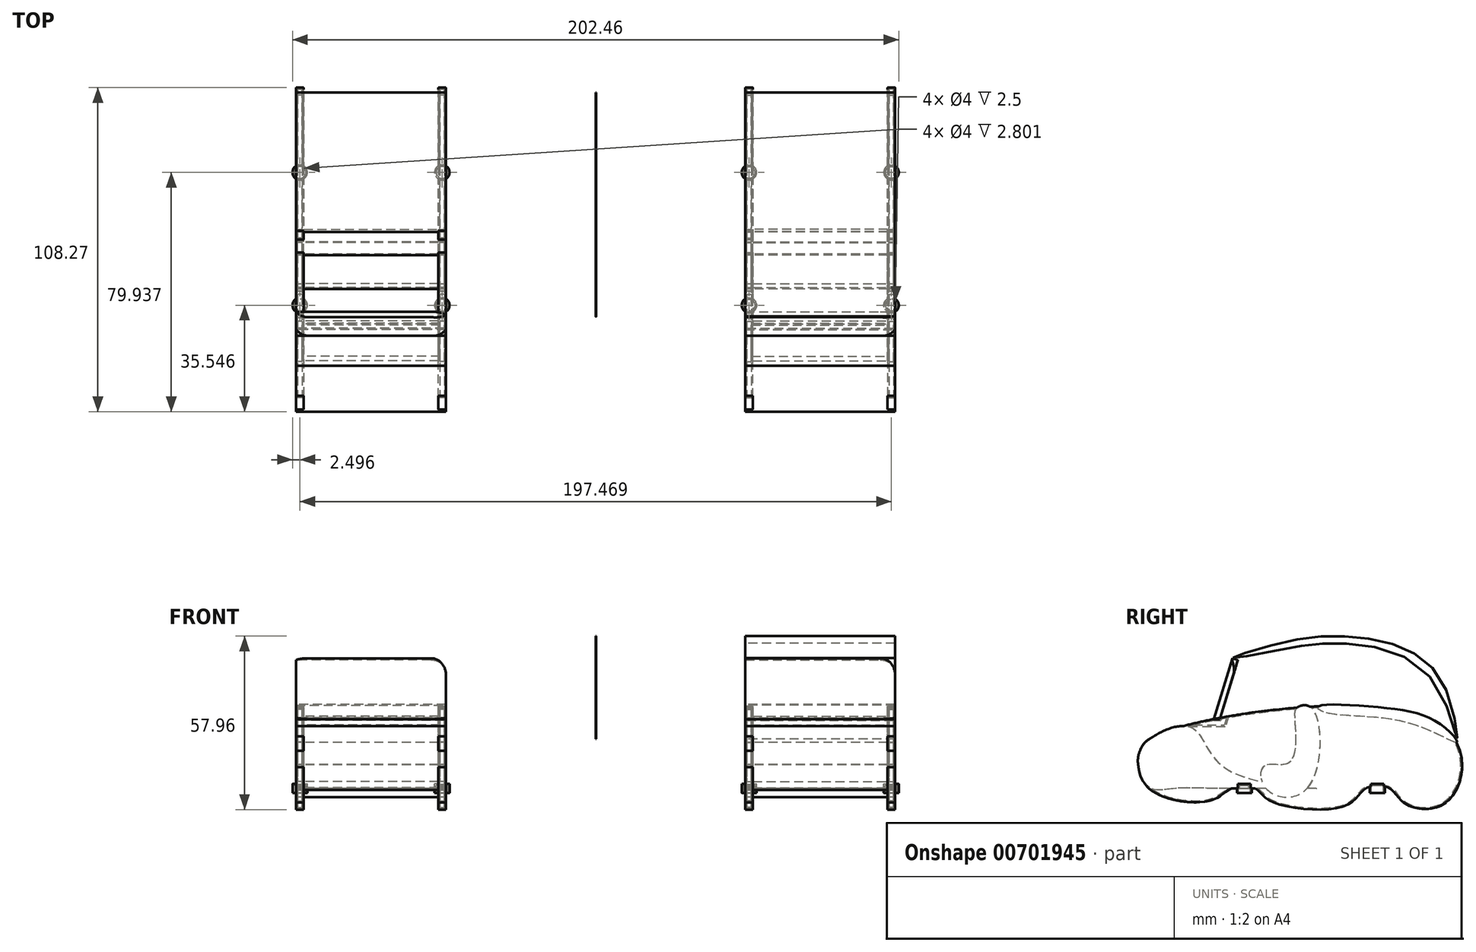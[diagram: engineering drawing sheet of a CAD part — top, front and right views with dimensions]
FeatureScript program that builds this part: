
annotation { "Feature Type Name" : "Feature", "Feature Type Description" : "" }
export const myFeature = defineFeature(function(context is Context, id is Id, definition is map)
    precondition{}
    {
        {
            var Q0;
            Q0=qCreatedBy(makeId("Right.planeOp"),FACE);
            var sketch = newSketch(context, id + "F0", { "sketchPlane" : qUnion([Q0])});
            skFitSpline(sketch, "E0", {"points": [v(-51.6, 18.76) * mm, v(-59.76, 11.07) * mm, v(-56.5, 0) * mm, v(-36, -4.08) * mm, v(-28.77, 0) * mm, v(-20.85, 0) * mm, v(-16.2, -4.08) * mm, v(9.44, -5.7) * mm, v(15.96, 0) * mm, v(23.88, 0) * mm, v(29, -5) * mm, v(43.22, -4.31) * mm, v(42.05, 20.39) * mm, v(-51.6, 18.76) * mm]});
            skLineSegment(sketch, "E1", {"start": v(-34.79, 23.16) * mm, "end": v(-28.6, 43.48) * mm});
            skLineSegment(sketch, "E2", {"start": v(-28.6, 43.48) * mm, "end": v(-26.72, 42.9) * mm});
            skLineSegment(sketch, "E3", {"start": v(-26.72, 42.9) * mm, "end": v(-32.74, 23.16) * mm});
            skLineSegment(sketch, "E4", {"start": v(-34.79, 23.16) * mm, "end": v(-32.74, 23.16) * mm});
            skSolve(sketch);
        }
        {
            var Q0;
            {var subQ0=sQuery(id+"F0.wireOp",EDGE,"E4");Q0=makeQuery(id+"F0.imprint","IMPRINT",FACE,{"disambiguationData":[TD([[makeQuery(id+"F0.imprint","IMPRINT",EDGE,{"derivedFrom":subQ0}),-1.0]])]});}
            var Q1;
            {var subQ0=sQuery(id+"F0.wireOp",EDGE,"E1");Q1=makeQuery(id+"F0.imprint","IMPRINT",FACE,{"disambiguationData":[TD([[makeQuery(id+"F0.imprint","IMPRINT",EDGE,{"derivedFrom":subQ0}),-1.0]])]});}
            extrude(context, id + "F1", {"entities" : qUnion([Q0, Q1]), "endBound" : BoundingType.SYMMETRIC, "depth" : 50 * mm, "offsetDistance" : 25 * mm});
        }
        {
            var Q0;
            {var subQ0=sQuery(id+"F0.wireOp",EDGE,"E0");Q0=makeQuery(id+"F1.opExtrude","SWEPT_FACE",FACE,{"disambiguationData":[OSD([subQ0]),TDD([makeQuery(id+"F0.imprint","IMPRINT",EDGE,{"disambiguationData":[TD([[makeQuery(id+"F0.imprint","INTERSECT",VERTEX,{"derivedFrom":[subQ0,sQuery(id+"F0.wireOp",EDGE,"E3")]}),1.0]])],"derivedFrom":subQ0})])]});}
            shell(context, id + "F2", {"entities" : qUnion([Q0]), "thickness" : 2.5 * mm});
        }
        {
            var Q0;
            Q0=qCreatedBy(makeId("Top.planeOp"),FACE);
            var sketch = newSketch(context, id + "F3", { "sketchPlane" : qUnion([Q0])});
            skCircle(sketch, "E5", {"center": v(-23.73, 19.8) * mm, "radius": 2.5 * mm});
            skCircle(sketch, "E6", {"center": v(-23.73, -24.6) * mm, "radius": 2.5 * mm});
            skCircle(sketch, "E7.MirrorC", {"center": v(23.73, -24.6) * mm, "radius": 2.5 * mm});
            skCircle(sketch, "E8.MirrorC", {"center": v(23.73, 19.8) * mm, "radius": 2.5 * mm});
            skSolve(sketch);
        }
        {
            var Q0;
            Q0 = qSketchRegion(id + "F3", true);
            extrude(context, id + "F4", {"entities" : qUnion([Q0]), "operationType" : NewBodyOperationType.ADD, "endBound" : BoundingType.SYMMETRIC, "oppositeDirection" : true, "depth" : 3 * mm, "offsetDistance" : 25 * mm});
        }
        {
            var Q0;
            Q0=makeQuery(id+"F4.opExtrude","CAP_FACE",FACE,{"disambiguationData":[OSD([sQuery(id+"F3.wireOp",EDGE,"E6")])],"isStart":false});
            var Q1;
            Q1=makeQuery(id+"F4.opExtrude","CAP_FACE",FACE,{"disambiguationData":[OSD([sQuery(id+"F3.wireOp",EDGE,"E7.MirrorC")])],"isStart":false});
            var Q2;
            Q2=makeQuery(id+"F4.opExtrude","CAP_FACE",FACE,{"disambiguationData":[OSD([sQuery(id+"F3.wireOp",EDGE,"E8.MirrorC")])],"isStart":false});
            var Q3;
            Q3=makeQuery(id+"F4.opExtrude","CAP_FACE",FACE,{"disambiguationData":[OSD([sQuery(id+"F3.wireOp",EDGE,"E5")])],"isStart":false});
            shell(context, id + "F5", {"entities" : qUnion([Q0, Q1, Q2, Q3]), "thickness" : 0.5 * mm});
        }
        {
            var Q0;
            Q0=qCreatedBy(makeId("Right.planeOp"),FACE);
            var sketch = newSketch(context, id + "F6", { "sketchPlane" : qUnion([Q0])});
            skFitSpline(sketch, "E9", {"points": [v(-6.9, 27.02) * mm, v(-7.77, 23.08) * mm, v(-9.52, 8.64) * mm, v(-17.83, 7.55) * mm, v(-17.4, 0) * mm, v(-3.6, 0) * mm, v(-1.86, 26.58) * mm, v(-6.9, 27.02) * mm]});
            skSolve(sketch);
        }
        {
            var Q0;
            Q0 = qSketchRegion(id + "F6", true);
            extrude(context, id + "F7", {"entities" : qUnion([Q0]), "operationType" : NewBodyOperationType.ADD, "endBound" : BoundingType.SYMMETRIC, "depth" : 50 * mm, "offsetDistance" : 25 * mm});
        }
        {
            var Q0;
            Q0=qCreatedBy(makeId("Right.planeOp"),FACE);
            var sketch = newSketch(context, id + "F8", { "sketchPlane" : qUnion([Q0])});
            skFitSpline(sketch, "E10", {"points": [v(0, 27.23) * mm, v(20.9, 27.02) * mm, v(40.8, 21.55) * mm, v(46.48, 15.42) * mm, v(30.52, 21.77) * mm, v(2.73, 25.27) * mm, v(0, 27.23) * mm]});
            skSolve(sketch);
        }
        {
            var Q0;
            Q0 = qSketchRegion(id + "F8", true);
            extrude(context, id + "F9", {"entities" : qUnion([Q0]), "operationType" : NewBodyOperationType.ADD, "endBound" : BoundingType.SYMMETRIC, "depth" : 50 * mm, "offsetDistance" : 25 * mm});
        }
        {
            var Q0;
            Q0=qCreatedBy(makeId("Right.planeOp"),FACE);
            var sketch = newSketch(context, id + "F10", { "sketchPlane" : qUnion([Q0])});
            skFitSpline(sketch, "E11", {"points": [v(41.9, 18.27) * mm, v(47.36, 12.36) * mm, v(47.8, 6.23) * mm, v(45.83, 0) * mm, v(42.1, 0) * mm, v(27.9, 0) * mm, v(21.1, 0) * mm, v(1.64, 0) * mm, v(0, 0) * mm, v(41.9, 18.27) * mm]});
            skSolve(sketch);
        }
        {
            var Q0;
            Q0=sQuery(id+"F10.wireOp",EDGE,"E11");
            extrude(context, id + "F11", {"bodyType" : ToolBodyType.SURFACE, "surfaceEntities" : qUnion([Q0]), "endBound" : BoundingType.SYMMETRIC, "depth" : 50 * mm, "offsetDistance" : 25 * mm});
        }
        {
            var Q0;
            Q0=qCreatedBy(makeId("Right.planeOp"),FACE);
            var sketch = newSketch(context, id + "F12", { "sketchPlane" : qUnion([Q0])});
            skFitSpline(sketch, "E12", {"points": [v(0, 0) * mm, v(-12.8, 0) * mm, v(-24.6, 0) * mm, v(-35.98, 0) * mm, v(-47.36, 0) * mm, v(-55.9, 0) * mm, v(-59.6, 5.8) * mm, v(-58.3, 14.33) * mm, v(-42.55, 20.45) * mm, v(-30.52, 6.45) * mm, v(0, 0) * mm]});
            skSolve(sketch);
        }
        {
            var Q0;
            Q0 = qSketchRegion(id + "F12", true);
            extrude(context, id + "F13", {"entities" : qUnion([Q0]), "operationType" : NewBodyOperationType.ADD, "endBound" : BoundingType.SYMMETRIC, "depth" : 50 * mm, "offsetDistance" : 25 * mm});
        }
        {
            var Q0;
            Q0=qCreatedBy(makeId("Right.planeOp"),FACE);
            cPlane(context, id + "F14", {"entities" : qUnion([Q0]), "cplaneType" : CPlaneType.OFFSET, "offset" : 75 * mm, "width" : 150 * mm, "height" : 150 * mm});
        }
        {
            var Q0;
            Q0=makeQuery(id+"F1.opExtrude","SWEPT_BODY",BODY,{"disambiguationData":[OSD([sQuery(id+"F0.wireOp",EDGE,"E0"),sQuery(id+"F0.wireOp",EDGE,"E1"),sQuery(id+"F0.wireOp",EDGE,"E2"),sQuery(id+"F0.wireOp",EDGE,"E3")])]});
            var Q1;
            Q1=makeQuery(id+"F1.opExtrude","SWEPT_BODY",BODY,{"disambiguationData":[OSD([sQuery(id+"F0.wireOp",EDGE,"E0"),sQuery(id+"F0.wireOp",EDGE,"E3"),sQuery(id+"F0.wireOp",EDGE,"E4")])]});
            var Q2;
            Q2=makeQuery(id+"F11.opExtrude","SWEPT_BODY",BODY,{"disambiguationData":[OSD([sQuery(id+"F10.wireOp",EDGE,"E11")])]});
            var Q3;
            Q3=qCreatedBy(id+"F14.planeOp",FACE);
            mirror(context, id + "F15", {"entities" : qUnion([Q0, Q1, Q2]), "mirrorPlane" : qUnion([Q3])});
        }
        {
            var Q0;
            Q0=qCreatedBy(id+"F14.planeOp",FACE);
            var sketch = newSketch(context, id + "F16", { "sketchPlane" : qUnion([Q0])});
            skFitSpline(sketch, "E13", {"points": [v(-28.33, 43.64) * mm, v(-13.93, 48.23) * mm, v(7.5, 50.86) * mm, v(27.85, 47.14) * mm, v(42.55, 33.36) * mm, v(46.48, 16.52) * mm, v(37.52, 37.08) * mm, v(8.2, 48.45) * mm, v(-10.6, 46.7) * mm, v(-28.33, 43.64) * mm]});
            skSolve(sketch);
        }
        {
            var Q0;
            Q0 = qSketchRegion(id + "F16", true);
            extrude(context, id + "F17", {"entities" : qUnion([Q0]), "depth" : 100 * mm, "offsetDistance" : 25 * mm});
        }
        {
            var Q0;
            Q0=qCreatedBy(makeId("Front.planeOp"),FACE);
            var sketch = newSketch(context, id + "F18", { "sketchPlane" : qUnion([Q0])});
            skLineSegment(sketch, "E14", {"start": v(124.92, 15.86) * mm, "end": v(124.92, 60.7) * mm});
            skLineSegment(sketch, "E15", {"start": v(124.92, 60.7) * mm, "end": v(75.23, 60.7) * mm});
            skLineSegment(sketch, "E16", {"start": v(75.23, 60.7) * mm, "end": v(75.23, 15.2) * mm});
            skLineSegment(sketch, "E17", {"start": v(75.23, 15.2) * mm, "end": v(124.92, 15.86) * mm});
            skSolve(sketch);
        }
        {
            var Q0;
            Q0=makeQuery(id+"F18.imprint","IMPRINT",FACE,{"disambiguationData":[TD([[makeQuery(id+"F18.imprint","IMPRINT",EDGE,{"derivedFrom":sQuery(id+"F18.wireOp",EDGE,"E14")}),1.0]])]});
            extrude(context, id + "F19", {"entities" : qUnion([Q0]), "operationType" : NewBodyOperationType.REMOVE, "endBound" : BoundingType.SYMMETRIC, "depth" : 100 * mm, "offsetDistance" : 25 * mm});
        }
        {
            var Q0;
            Q0=qCreatedBy(makeId("Front.planeOp"),FACE);
            cPlane(context, id + "F20", {"entities" : qUnion([Q0]), "cplaneType" : CPlaneType.OFFSET, "offset" : 46.3 * mm, "oppositeDirection" : true, "width" : 150 * mm, "height" : 150 * mm});
        }
        {
            var Q0;
            Q0=qCreatedBy(id+"F20.planeOp",FACE);
            var sketch = newSketch(context, id + "F21", { "sketchPlane" : qUnion([Q0])});
            skCircle(sketch, "E18", {"center": v(11.86, 7.28) * mm, "radius": 7.4 * mm});
            skSolve(sketch);
        }
        {
            var Q0;
            Q0=sQuery(id+"F21.wireOp",EDGE,"E18");
            extrude(context, id + "F22", {"bodyType" : ToolBodyType.SURFACE, "surfaceEntities" : qUnion([Q0]), "oppositeDirection" : true, "depth" : 3 * mm, "offsetDistance" : 25 * mm});
        }
        {
            var Q0;
            Q0=makeQuery(id+"F22.opExtrude","SWEPT_BODY",BODY,{"disambiguationData":[OSD([sQuery(id+"F21.wireOp",EDGE,"E18")])]});
            var Q1;
            Q1=qCreatedBy(makeId("Right.planeOp"),FACE);
            mirror(context, id + "F23", {"entities" : qUnion([Q0]), "mirrorPlane" : qUnion([Q1])});
        }
        {
            var Q0;
            Q0=makeQuery(id+"F22.opExtrude","SWEPT_BODY",BODY,{"disambiguationData":[OSD([sQuery(id+"F21.wireOp",EDGE,"E18")])]});
            var Q1;
            Q1=makeQuery(id+"F23.opPattern","COPY",BODY,{"derivedFrom":makeQuery(id+"F22.opExtrude","SWEPT_BODY",BODY,{"disambiguationData":[OSD([sQuery(id+"F21.wireOp",EDGE,"E18")])]}),"instanceName":"1"});
            var Q2;
            Q2=qCreatedBy(id+"F14.planeOp",FACE);
            mirror(context, id + "F24", {"entities" : qUnion([Q0, Q1]), "mirrorPlane" : qUnion([Q2])});
        }
        {
            var Q0;
            Q0=makeQuery(id+"F15.opPattern","COPY",EDGE,{"derivedFrom":makeQuery(id+"F1.opExtrude","CAP_EDGE",EDGE,{"disambiguationData":[OSD([sQuery(id+"F0.wireOp",EDGE,"E1")])],"isStart":true}),"instanceName":"1"});
            var Q1;
            Q1=makeQuery(id+"F15.opPattern","COPY",EDGE,{"derivedFrom":makeQuery(id+"F1.opExtrude","CAP_EDGE",EDGE,{"disambiguationData":[OSD([sQuery(id+"F0.wireOp",EDGE,"E2")])],"isStart":true}),"instanceName":"1"});
            fillet(context, id + "F25", {"entities" : qUnion([Q0, Q1]), "radius" : 5 * mm, "tangentPropagation" : true, "allowEdgeOverflow" : false});
        }
        {
            var Q0;
            Q0=makeQuery(id+"F1.opExtrude","CAP_EDGE",EDGE,{"disambiguationData":[OSD([sQuery(id+"F0.wireOp",EDGE,"E1")])],"isStart":false});
            var Q1;
            Q1=makeQuery(id+"F1.opExtrude","CAP_EDGE",EDGE,{"disambiguationData":[OSD([sQuery(id+"F0.wireOp",EDGE,"E1")])],"isStart":true});
            var Q2;
            Q2=makeQuery(id+"F1.opExtrude","CAP_EDGE",EDGE,{"disambiguationData":[OSD([sQuery(id+"F0.wireOp",EDGE,"E2")])],"isStart":false});
            fillet(context, id + "F26", {"entities" : qUnion([Q0, Q1, Q2]), "radius" : 5 * mm, "tangentPropagation" : true, "allowEdgeOverflow" : false});
        }
    });
